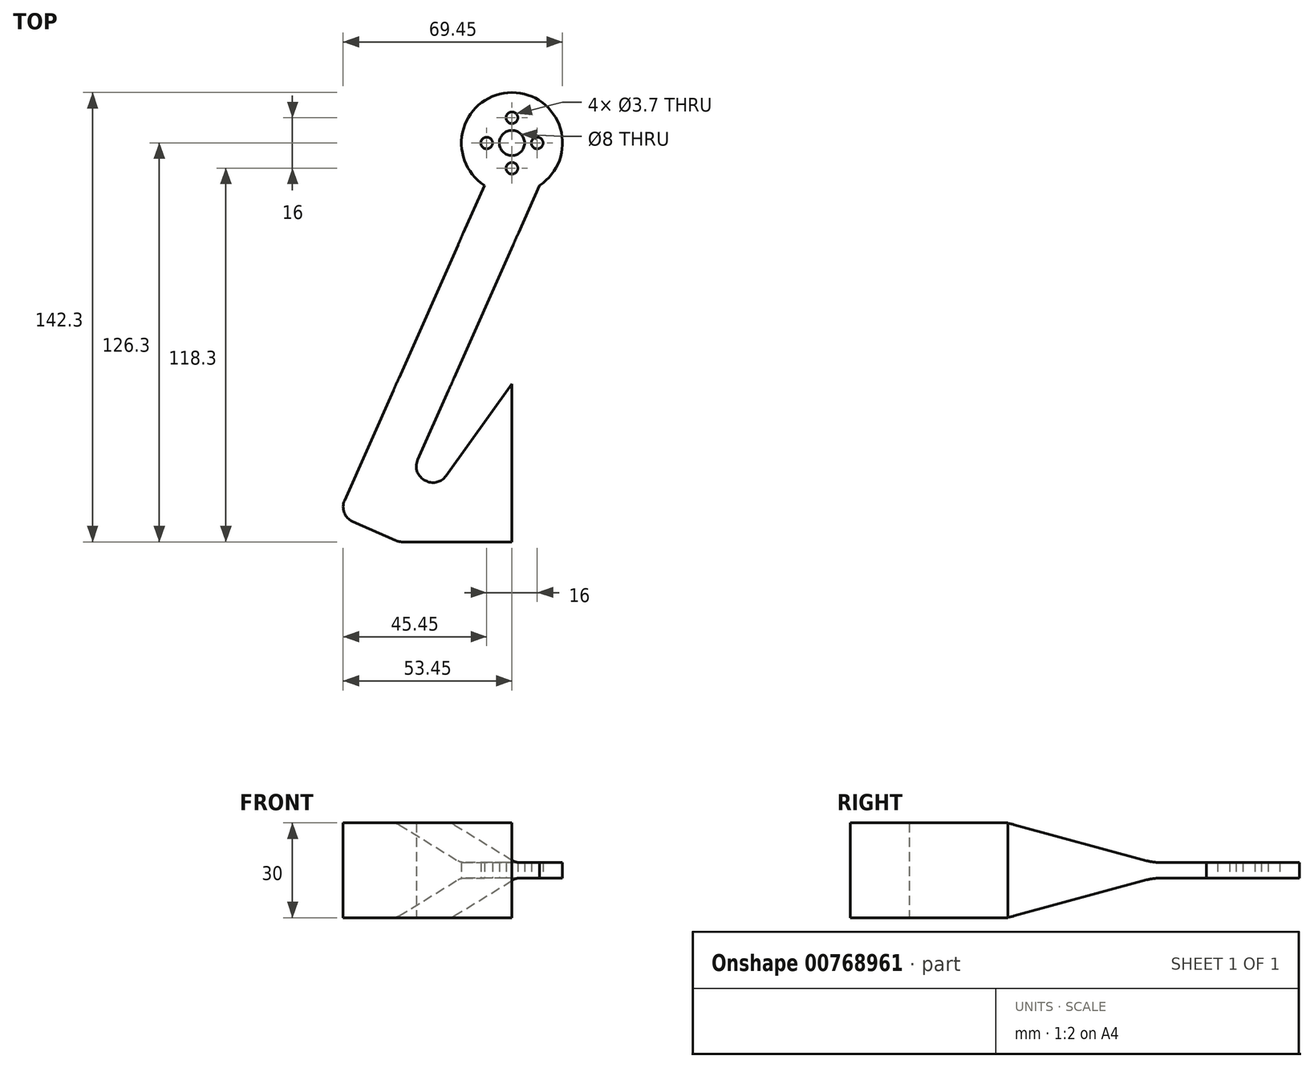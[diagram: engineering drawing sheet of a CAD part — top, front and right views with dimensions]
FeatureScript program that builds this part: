
annotation { "Feature Type Name" : "Feature", "Feature Type Description" : "" }
export const myFeature = defineFeature(function(context is Context, id is Id, definition is map)
    precondition{}
    {
        {
            var Q0;
            Q0=qCreatedBy(makeId("Top.planeOp"),FACE);
            var sketch = newSketch(context, id + "F0", { "sketchPlane" : qUnion([Q0])});
            skCircle(sketch, "E0", {"center": v(0, 45.18) * mm, "radius": 16 * mm, "construction": true});
            skCircle(sketch, "E1", {"center": v(0, 45.18) * mm, "radius": 4 * mm});
            skCircle(sketch, "E2", {"center": v(0, 53.18) * mm, "radius": 1.85 * mm});
            skCircle(sketch, "E3.1.0", {"center": v(-8, 45.18) * mm, "radius": 1.85 * mm});
            skCircle(sketch, "E3.2.0", {"center": v(0, 37.18) * mm, "radius": 1.85 * mm});
            skCircle(sketch, "E3.3.0", {"center": v(8, 45.18) * mm, "radius": 1.85 * mm});
            skLineSegment(sketch, "E4", {"start": v(0, -31.12) * mm, "end": v(0, -81.12) * mm});
            skLineSegment(sketch, "E5", {"start": v(0, -81.12) * mm, "end": v(-34.83, -81.12) * mm});
            skLineSegment(sketch, "E6", {"start": v(-36.86, -80.69) * mm, "end": v(-50.48, -74.64) * mm});
            skLineSegment(sketch, "E7", {"start": v(-53.02, -68.05) * mm, "end": v(-8.73, 31.77) * mm});
            skLineSegment(sketch, "E8", {"start": v(8.74, 31.78) * mm, "end": v(-29.85, -55.2) * mm});
            skLineSegment(sketch, "E9", {"start": v(-27.31, -61.8) * mm, "end": v(-27.01, -61.92) * mm});
            skLineSegment(sketch, "E10", {"start": v(-20.92, -60.27) * mm, "end": v(0, -31.12) * mm});
            skPoint(sketch, "E11.visualSharp", {"position": v(-31.88, -59.76) * mm});
            skArc(sketch, "E11.filletArc", {"start": v(-29.85, -55.2) * mm, "mid": v(-29.95, -59.02) * mm, "end": v(-27.31, -61.8) * mm});
            skPoint(sketch, "E12.visualSharp", {"position": v(-23.3, -63.57) * mm});
            skArc(sketch, "E12.filletArc", {"start": v(-27.01, -61.92) * mm, "mid": v(-23.67, -62.18) * mm, "end": v(-20.92, -60.27) * mm});
            skPoint(sketch, "E13.visualSharp", {"position": v(-35.9, -81.12) * mm});
            skArc(sketch, "E13.filletArc", {"start": v(-36.86, -80.69) * mm, "mid": v(-35.87, -81) * mm, "end": v(-34.83, -81.12) * mm});
            skPoint(sketch, "E14.visualSharp", {"position": v(-55.05, -72.62) * mm});
            skArc(sketch, "E14.filletArc", {"start": v(-53.02, -68.05) * mm, "mid": v(-53.12, -71.87) * mm, "end": v(-50.48, -74.64) * mm});
            skArc(sketch, "E15", {"start": v(8.74, 31.78) * mm, "mid": v(0, 61.18) * mm, "end": v(-8.73, 31.77) * mm});
            skLineSegment(sketch, "E16", {"start": v(-19.17, -31.12) * mm, "end": v(-36.64, -31.12) * mm});
            skLineSegment(sketch, "E17", {"start": v(1.2, 14.8) * mm, "end": v(-16.26, 14.8) * mm});
            skSolve(sketch);
        }
        {
            var Q0;
            Q0=makeQuery(id+"F0.imprint","IMPRINT",FACE,{"disambiguationData":[TD([[makeQuery(id+"F0.imprint","IMPRINT",EDGE,{"derivedFrom":sQuery(id+"F0.wireOp",EDGE,"E1")}),-1.0]])]});
            extrude(context, id + "F1", {"entities" : qUnion([Q0]), "endBound" : BoundingType.SYMMETRIC, "depth" : 5 * mm, "offsetDistance" : 25 * mm});
        }
        {
            var Q0;
            Q0=makeQuery(id+"F0.imprint","IMPRINT",FACE,{"disambiguationData":[TD([[makeQuery(id+"F0.imprint","IMPRINT",EDGE,{"derivedFrom":sQuery(id+"F0.wireOp",EDGE,"E4")}),-1.0]])]});
            extrude(context, id + "F2", {"entities" : qUnion([Q0]), "endBound" : BoundingType.SYMMETRIC, "depth" : 30 * mm, "offsetDistance" : 25 * mm});
        }
        {
            var Q0;
            Q0=makeQuery(id+"F2.opExtrude","SWEPT_FACE",FACE,{"disambiguationData":[OSD([sQuery(id+"F0.wireOp",EDGE,"E16")])]});
            var Q1;
            Q1=makeQuery(id+"F1.opExtrude","SWEPT_FACE",FACE,{"disambiguationData":[OSD([sQuery(id+"F0.wireOp",EDGE,"E17")])]});
            loft(context, id + "F3", {"sheetProfilesArray" : [{ "sheetProfileEntities" : qUnion([Q0]) }, { "sheetProfileEntities" : qUnion([Q1]) }]});
        }
        {
            var Q0;
            Q0=makeQuery(id+"F2.opExtrude","SWEPT_BODY",BODY,{"disambiguationData":[OSD([sQuery(id+"F0.wireOp",EDGE,"E4"),sQuery(id+"F0.wireOp",EDGE,"E5"),sQuery(id+"F0.wireOp",EDGE,"E6"),sQuery(id+"F0.wireOp",EDGE,"E7"),sQuery(id+"F0.wireOp",EDGE,"E8"),sQuery(id+"F0.wireOp",EDGE,"E9"),sQuery(id+"F0.wireOp",EDGE,"E10"),sQuery(id+"F0.wireOp",EDGE,"E11.filletArc"),sQuery(id+"F0.wireOp",EDGE,"E12.filletArc"),sQuery(id+"F0.wireOp",EDGE,"E13.filletArc"),sQuery(id+"F0.wireOp",EDGE,"E14.filletArc"),sQuery(id+"F0.wireOp",EDGE,"E16")])]});
            var Q1;
            Q1=makeQuery(id+"F3.opLoft","SWEPT_BODY",BODY,{"disambiguationData":[OSD([sQuery(id+"F0.wireOp",EDGE,"E16"),sQuery(id+"F0.wireOp",EDGE,"E17")])]});
            var Q2;
            Q2=makeQuery(id+"F1.opExtrude","SWEPT_BODY",BODY,{"disambiguationData":[OSD([sQuery(id+"F0.wireOp",EDGE,"E1"),sQuery(id+"F0.wireOp",EDGE,"E2"),sQuery(id+"F0.wireOp",EDGE,"E3.1.0"),sQuery(id+"F0.wireOp",EDGE,"E3.2.0"),sQuery(id+"F0.wireOp",EDGE,"E3.3.0"),sQuery(id+"F0.wireOp",EDGE,"E7"),sQuery(id+"F0.wireOp",EDGE,"E8"),sQuery(id+"F0.wireOp",EDGE,"E15"),sQuery(id+"F0.wireOp",EDGE,"E17")])]});
            booleanBodies(context, id + "F4", {"operationType" : BooleanOperationType.UNION, "tools" : qUnion([Q0, Q1, Q2])});
        }
        {
            var Q0;
            {var subQ0=sQuery(id+"F0.wireOp",EDGE,"E16");var subQ1=makeQuery(id+"F2.opExtrude","CAP_EDGE",EDGE,{"disambiguationData":[OSD([subQ0])],"isStart":false});var subQ2=sQuery(id+"F0.wireOp",EDGE,"E7");var subQ3=sQuery(id+"F0.wireOp",EDGE,"E8");Q0=makeQuery(id+"F4.opBoolean","MERGE",EDGE,{"derivedFrom":[subQ1,makeQuery(id+"F3.opLoft","MID_CAP_EDGE",EDGE,{"disambiguationData":[OSD([subQ2,subQ3,subQ0]),TDD([makeQuery(id+"F2.opExtrude","CAP_VERTEX",VERTEX,{"disambiguationData":[OSD([subQ3,subQ0])],"isStart":false}),makeQuery(id+"F2.opExtrude","CAP_VERTEX",VERTEX,{"disambiguationData":[OSD([subQ2,subQ0])],"isStart":false}),subQ1])],"capPos":0.0})]});}
            var Q1;
            {var subQ0=sQuery(id+"F0.wireOp",EDGE,"E16");var subQ1=makeQuery(id+"F2.opExtrude","CAP_EDGE",EDGE,{"disambiguationData":[OSD([subQ0])],"isStart":true});var subQ2=sQuery(id+"F0.wireOp",EDGE,"E7");var subQ3=sQuery(id+"F0.wireOp",EDGE,"E8");Q1=makeQuery(id+"F4.opBoolean","MERGE",EDGE,{"derivedFrom":[subQ1,makeQuery(id+"F3.opLoft","MID_CAP_EDGE",EDGE,{"disambiguationData":[OSD([subQ2,subQ3,subQ0]),TDD([makeQuery(id+"F2.opExtrude","CAP_VERTEX",VERTEX,{"disambiguationData":[OSD([subQ3,subQ0])],"isStart":true}),makeQuery(id+"F2.opExtrude","CAP_VERTEX",VERTEX,{"disambiguationData":[OSD([subQ2,subQ0])],"isStart":true}),subQ1])],"capPos":0.0})]});}
            var Q2;
            {var subQ0=sQuery(id+"F0.wireOp",EDGE,"E17");var subQ1=makeQuery(id+"F1.opExtrude","CAP_EDGE",EDGE,{"disambiguationData":[OSD([subQ0])],"isStart":true});var subQ2=sQuery(id+"F0.wireOp",EDGE,"E7");var subQ3=sQuery(id+"F0.wireOp",EDGE,"E8");Q2=makeQuery(id+"F4.opBoolean","MERGE",EDGE,{"derivedFrom":[subQ1,makeQuery(id+"F3.opLoft","MID_CAP_EDGE",EDGE,{"disambiguationData":[OSD([subQ2,subQ3,subQ0]),TDD([makeQuery(id+"F1.opExtrude","CAP_VERTEX",VERTEX,{"disambiguationData":[OSD([subQ3,subQ0])],"isStart":true}),makeQuery(id+"F1.opExtrude","CAP_VERTEX",VERTEX,{"disambiguationData":[OSD([subQ2,subQ0])],"isStart":true}),subQ1])],"capPos":1.0})]});}
            var Q3;
            {var subQ0=sQuery(id+"F0.wireOp",EDGE,"E17");var subQ1=makeQuery(id+"F1.opExtrude","CAP_EDGE",EDGE,{"disambiguationData":[OSD([subQ0])],"isStart":false});var subQ2=sQuery(id+"F0.wireOp",EDGE,"E7");var subQ3=sQuery(id+"F0.wireOp",EDGE,"E8");Q3=makeQuery(id+"F4.opBoolean","MERGE",EDGE,{"derivedFrom":[subQ1,makeQuery(id+"F3.opLoft","MID_CAP_EDGE",EDGE,{"disambiguationData":[OSD([subQ2,subQ3,subQ0]),TDD([makeQuery(id+"F1.opExtrude","CAP_VERTEX",VERTEX,{"disambiguationData":[OSD([subQ3,subQ0])],"isStart":false}),makeQuery(id+"F1.opExtrude","CAP_VERTEX",VERTEX,{"disambiguationData":[OSD([subQ2,subQ0])],"isStart":false}),subQ1])],"capPos":1.0})]});}
            fillet(context, id + "F5", {"entities" : qUnion([Q0, Q1, Q2, Q3]), "radius" : 15 * mm, "tangentPropagation" : true, "allowEdgeOverflow" : false});
        }
    });
